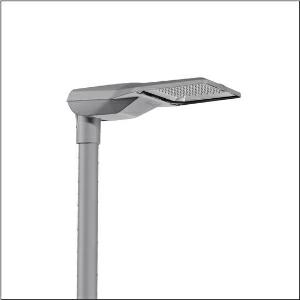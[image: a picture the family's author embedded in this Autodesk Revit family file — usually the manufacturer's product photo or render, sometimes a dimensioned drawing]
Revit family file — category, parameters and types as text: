
# Revit family: streetlight_sl_21_iq_midi___st1_0a_5xe3d61g08nb_ea68
name_source: partatom
category: Lighting Fixtures
units: mm (PartAtom-declared; Revit-internal decimal feet)

## family parameters
Cut with Voids When Loaded = No
Host = Face
Light Source = No
Part Type = Normal
Room Calculation Point = No
Round Connector Dimension = Use Diameter
Shared = No

## types (1)
- --- (1 x LED, 20820 lm, 155.5 W, 2700K)
    Apparent Load = 155 VA
    CIE Flux Codes = 40 73 97 100 100
    Color Rendering = 70
    Color Temperature = 2700K
    Default Elevation = 1800 mm
    Description = Streetlight SL 21 iQ midi, mast luminaire, primary light control with lens, of PMMA, primary optical cover: cover, of toughened safety glass, transparent, light distribution: ST1.0a, light emission: direct distribution, primary light characteristic: asymmetric, installation type: post-top, side-entry, LED, High Power LED, rated luminous flux: 20.820lm, luminous efficacy: 134lm/W, light colour: 727, colour temperature: 2700K, control: Street-Remote, Auto-Match, Temp-Guard, Lumen-Switch, Night-Set, Smart-Wire, Light-Fading, Desk-Remote (wireless, voltage-free reading and setting of iQ features in the workshop via application-optimized NFC function/RFID function), optimised constant luminous flux control (CLO 2.0), presetting dimming linear, mains connection: 230..240V, AC, 50/60Hz, start of lifetime: 156W, end of service life: 162W, reduction: 69W, luminaire housing, of diecast aluminium, powder-coated, Siteco® metallic grey (DB 702S), corrosivity category C5 mid according to DIN EN ISO 12944, please order mast flange separately, inclination adjustable: 0°, 5°, 10°, 15°, sealing non-destructively replaceable, multi-level sealing system, length: 644mm, width: 335mm, height: 110mm, mast flange for spigot size: 42mm (side-entry): 5XC10008XM4, 60/48mm (side-entry/post-top): 5XC10108XM2, 76/60mm (side-entry/post-top): 5XC10108XM1, protection rating (complete): IP66, insulation class (complete): insulation class II (safety insulation), certification: CE, ENEC, ENEC+, VDE, impact resistance: IK09, permissible operating ambient temperature for outdoor applications: -40..+50°C, standard-compliant lighting for roads and squares, packaging unit: 1 piece

Light Distribution: ST1.0a
    Height = 111 mm
    Lamp = 1 x LED
    Lamp Light Flux = 20820 lm
    Lamp Power = 155.5 W
    Lamp count = 1
    Length = 644 mm
    Luminous efficacy = 134 lm/W
    Manufacturer = Siteco
    ModVariant = No
    Model = 5XE3D61G08NB
    Number of Poles = 1
    OnlyDefault = Yes
    Power Factor = 1
    Product Name = Streetlight SL 21 iQ midi | ST1.0a
    Product group = mast luminaire | pylon top
    ProductGroupID = 6100
    Protection Class = Protection class II
    Protection Degree = IP 66
    RLX_Detail_Level = 1
    RLX_Emergency_Light_Flux = 0 lm
    RLX_Emergency_Type = 0
    RLX_Emergency_Type_DB = No
    RlxData = <blob elided: 90909 chars, md5=74c5f2f3>
    Socket = socket
    Standby Power = 0 W
    System Light Flux = 20820 lm
    System Power = 155 W
    Type Comments = factory setting: luminous flux: 100 % | dim-lin: 254 | 823 mA
    Type Image = l_1004298.jpg
    URL = http://relux.com
    VarID = @adj_103423
    Voltage = 0 V
    Weight = 0.00 kg
    Width = 336 mm

## geometry (parser evidence)
native form markers: Blend x4, Sweep x11
no freeform markers — native parametric forms only
